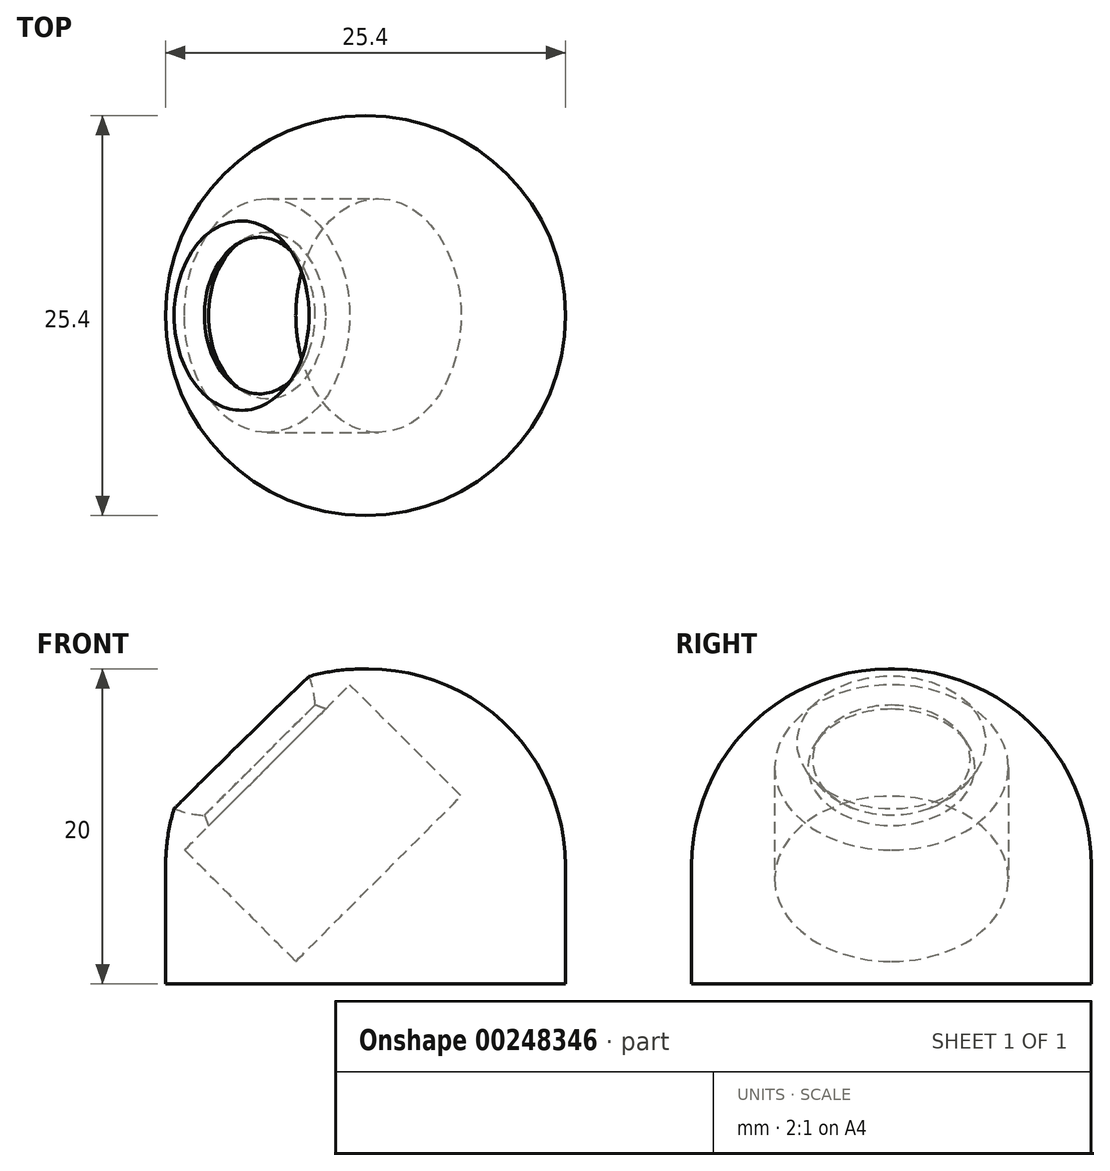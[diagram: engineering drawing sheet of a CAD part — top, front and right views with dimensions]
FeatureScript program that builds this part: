
annotation { "Feature Type Name" : "Feature", "Feature Type Description" : "" }
export const myFeature = defineFeature(function(context is Context, id is Id, definition is map)
    precondition{}
    {
        {
            var Q0;
            Q0=qCreatedBy(makeId("Top.planeOp"),FACE);
            var sketch = newSketch(context, id + "F0", { "sketchPlane" : qUnion([Q0])});
            skCircle(sketch, "E0", {"center": v(0, 0) * mm, "radius": 12.7 * mm});
            skSolve(sketch);
        }
        {
            var Q0;
            Q0 = qSketchRegion(id + "F0", true);
            extrude(context, id + "F1", {"entities" : qUnion([Q0]), "depth" : 20 * mm});
        }
        {
            var Q0;
            Q0=makeQuery(id+"F1.opExtrude","CAP_EDGE",EDGE,{"disambiguationData":[OSD([sQuery(id+"F0.wireOp",EDGE,"E0")])],"isStart":false});
            fillet(context, id + "F2", {"entities" : qUnion([Q0]), "radius" : 12.5 * mm, "tangentPropagation" : true, "allowEdgeOverflow" : false});
        }
        {
            var Q0;
            Q0=qCreatedBy(makeId("Front.planeOp"),FACE);
            var sketch = newSketch(context, id + "F3", { "sketchPlane" : qUnion([Q0])});
            skLineSegment(sketch, "E1", {"start": v(-1, 19) * mm, "end": v(-6.25, 13.75) * mm});
            skLineSegment(sketch, "E2", {"start": v(0.82, 6.68) * mm, "end": v(6.07, 11.93) * mm});
            skLineSegment(sketch, "E3", {"start": v(-1, 19) * mm, "end": v(6.07, 11.93) * mm});
            skLineSegment(sketch, "E4", {"start": v(-6.25, 13.75) * mm, "end": v(0.82, 6.68) * mm});
            skPoint(sketch, "E5.start.orphan", {"position": v(-11.5, 8.5) * mm});
            skPoint(sketch, "E6.orphan", {"position": v(-4.43, 1.43) * mm});
            skSolve(sketch);
        }
        {
            var Q0;
            Q0 = qSketchRegion(id + "F3", true);
            var Q1;
            Q1=sQuery(id+"F3.wireOp",EDGE,"E4");
            revolve(context, id + "F4", {"operationType" : NewBodyOperationType.REMOVE, "entities" : qUnion([Q0]), "axis" : qUnion([Q1]), "revolveType" : RevolveType.FULL, "oppositeDirection" : true});
        }
        {
            var Q0;
            Q0=qCreatedBy(makeId("Front.planeOp"),FACE);
            var sketch = newSketch(context, id + "F5", { "sketchPlane" : qUnion([Q0])});
            skLineSegment(sketch, "E7.0", {"start": v(6.07, 11.93) * mm, "end": v(-4.43, 1.43) * mm});
            skLineSegment(sketch, "E8", {"start": v(0.82, 6.68) * mm, "end": v(-9.79, 17.29) * mm});
            skCircle(sketch, "E9", {"center": v(-9.79, 17.29) * mm, "radius": 6.6 * mm});
            skLineSegment(sketch, "E10", {"start": v(-9.79, 17.29) * mm, "end": v(-14.45, 21.95) * mm});
            skSolve(sketch);
        }
        {
            var Q0;
            {var subQ0=sQuery(id+"F5.wireOp",EDGE,"E10");Q0=makeQuery(id+"F5.imprint","IMPRINT",FACE,{"disambiguationData":[TD([[makeQuery(id+"F5.imprint","IMPRINT",EDGE,{"derivedFrom":subQ0}),-1.0]])]});}
            var Q1;
            Q1=sQuery(id+"F5.wireOp",EDGE,"E10");
            revolve(context, id + "F6", {"operationType" : NewBodyOperationType.REMOVE, "entities" : qUnion([Q0]), "axis" : qUnion([Q1]), "revolveType" : RevolveType.FULL, "oppositeDirection" : true});
        }
        {
            var Q0;
            Q0=makeQuery(id+"F6.boolean.opBoolean","INTERSECT",EDGE,{"derivedFrom":[makeQuery(id+"F4.boolean.opBoolean","COPY",FACE,{"derivedFrom":makeQuery(id+"F4.opRevolve","SWEPT_FACE",FACE,{"disambiguationData":[OSD([sQuery(id+"F3.wireOp",EDGE,"E1")])]})}),makeQuery(id+"F6.opRevolve","SWEPT_FACE",FACE,{"disambiguationData":[OSD([sQuery(id+"F5.wireOp",EDGE,"E9")])]})]});
            chamfer(context, id + "F7", {"entities" : qUnion([Q0]), "width" : 0.4 * mm, "tangentPropagation" : true});
        }
    });
